# Revit family: CircLED Bollard
name_source: partatom
category: Lighting Fixtures
revit_build: Autodesk Revit Architecture 2014 (Build: 20140709_2115(x64)
units: mm (PartAtom-declared; Revit-internal decimal feet)

## types (1)
- CircLED Bollard
    Apparent Load = 240 VA
    ArticleNumber = See URL hyperlink
    AssetType = Moveable/Fixed
    BIMObjectName = CircLED Bollard.rfa
    BSAB 96 = SNB.2
    BallastsCELMAEnergyEfficiencyIndex = Class A1/A2
    CCSClassCode = UAC
    CCSClassName = Belysningsarmatur
    CCSTopnode = L
    Color Filter = 16777215
    Colour = Black
    ControlGearPosition = Integrated
    Description = 70-80-35 General Lighting Systems
    Diameter 1 = 160 mm
    Diameter 2 = 220 mm
    Dimming Lamp Color Temperature Shift = <None>
    DocumentReference = See URL hyperlink
    Documentation = See URL hyperlink
    Finish = Powder coated
    Frame = Riegens_Aluminum_powder coated black
    HasProtectiveEarth = TRUE
    Height 1 = 900 mm
    Height 2 = 140 mm
    IP_Code = IP54
    IfcExportAs = IfcLightFixtureType'
    IfcExportType = NOTDEFINED'
    InsulationStandardClass = Class 1 / Class 2
    InternalFuse = Only required in emergency versions
    LampColourRenderingIndex = Ra>80
    LampRating = 16W
    LampType = LED
    LightFixtureMountingType = Surface
    LightFixturePlacingType = Other
    LightSource = LED 3000K
    LuminairePowerFactor = >0,9
    LuminaireType = Outdoor Indirect LED Luminaire
    Manufacturer = Riegens A/S
    ManufacturerURL = www.riegens.com
    Material = Aluminium and PC
    Model = CircLED Bollard
    ModelReference = CircLED Bollard
    NominalVoltage = 220-240V
    Optic = Mirror matt / Satin matt / Soft optic
    PhaseReference = IEC recommendations
    Photometric Web File = CircLED Bollard 16W 3000K Miirrormatt finish reflector Black structure IP54.ies
    PhotometricPerformance = In accordance with BS EN 13032-1
    ProductInformation = http://riegens.com
    Shape = Circle
    Size = Ø220 mm
    Tilt Angle = 90.00°
    TotalWattage = Max. 16W
    URL = http://riegens.com
    Uniclass 1.4 = JY73
    Uniclass2 = Pr_70_70_49_43 Light-Emitting Diode (LED) Luminaires
    Version = v.1.0

## geometry (parser evidence)
native form markers: Sweep x1
no freeform markers — native parametric forms only
